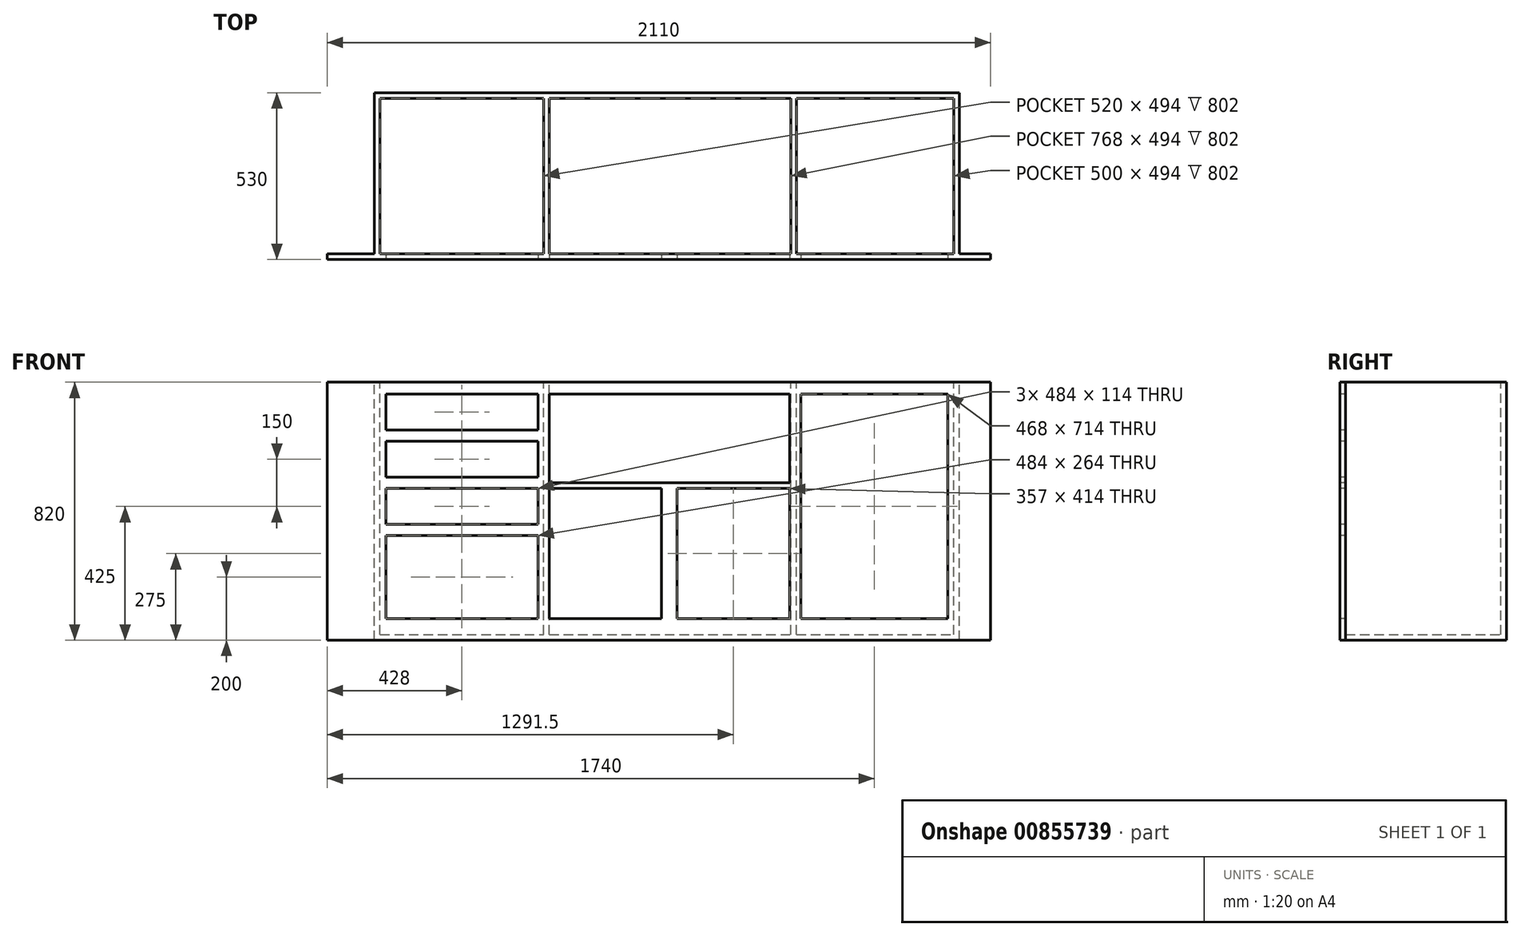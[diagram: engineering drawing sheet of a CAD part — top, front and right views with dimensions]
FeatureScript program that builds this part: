
annotation { "Feature Type Name" : "Feature", "Feature Type Description" : "" }
export const myFeature = defineFeature(function(context is Context, id is Id, definition is map)
    precondition{}
    {
        {
            var Q0;
            Q0=qCreatedBy(makeId("Top.planeOp"),FACE);
            var sketch = newSketch(context, id + "F0", { "sketchPlane" : qUnion([Q0])});
            skLineSegment(sketch, "E0.bottom", {"start": v(0, 0) * mm, "end": v(1860, 0) * mm});
            skLineSegment(sketch, "E0.top", {"start": v(0, 530) * mm, "end": v(1860, 530) * mm});
            skLineSegment(sketch, "E0.left", {"start": v(0, 18) * mm, "end": v(0, 530) * mm});
            skLineSegment(sketch, "E0.right", {"start": v(1860, 18) * mm, "end": v(1860, 530) * mm});
            skLineSegment(sketch, "E1.0", {"start": v(1842, 18) * mm, "end": v(1842, 512) * mm});
            skLineSegment(sketch, "E1.1", {"start": v(18, 18) * mm, "end": v(538, 18) * mm});
            skLineSegment(sketch, "E1.2", {"start": v(18, 18) * mm, "end": v(18, 512) * mm});
            skLineSegment(sketch, "E1.3", {"start": v(18, 512) * mm, "end": v(538, 512) * mm});
            skLineSegment(sketch, "E2.left", {"start": v(538, 512) * mm, "end": v(538, 18) * mm});
            skLineSegment(sketch, "E2.right", {"start": v(556, 512) * mm, "end": v(556, 18) * mm});
            skLineSegment(sketch, "E3.trimOffspring", {"start": v(556, 18) * mm, "end": v(1324, 18) * mm});
            skLineSegment(sketch, "E4.left", {"start": v(1342, 512) * mm, "end": v(1342, 18) * mm});
            skLineSegment(sketch, "E4.right", {"start": v(1324, 512) * mm, "end": v(1324, 18) * mm});
            skLineSegment(sketch, "E5.trimOffspring", {"start": v(1342, 18) * mm, "end": v(1842, 18) * mm});
            skLineSegment(sketch, "E6", {"start": v(0, 18) * mm, "end": v(-150, 18) * mm});
            skLineSegment(sketch, "E7", {"start": v(-150, 18) * mm, "end": v(-150, 0) * mm});
            skLineSegment(sketch, "E8", {"start": v(-150, 0) * mm, "end": v(0, 0) * mm});
            skLineSegment(sketch, "E9", {"start": v(1860, 0) * mm, "end": v(1960, 0) * mm});
            skLineSegment(sketch, "E10", {"start": v(1960, 0) * mm, "end": v(1960, 18) * mm});
            skLineSegment(sketch, "E11", {"start": v(1960, 18) * mm, "end": v(1860, 18) * mm});
            skLineSegment(sketch, "E12.trimOffspring", {"start": v(556, 512) * mm, "end": v(1324, 512) * mm});
            skLineSegment(sketch, "E13.trimOffspring", {"start": v(1342, 512) * mm, "end": v(1842, 512) * mm});
            skSolve(sketch);
        }
        {
            var Q0;
            Q0=makeQuery(id+"F0.imprint","IMPRINT",FACE,{"disambiguationData":[TD([[makeQuery(id+"F0.imprint","IMPRINT",EDGE,{"derivedFrom":sQuery(id+"F0.wireOp",EDGE,"E0.bottom")}),1.0]])]});
            var Q1;
            Q1=makeQuery(id+"F0.imprint","IMPRINT",FACE,{"disambiguationData":[TD([[makeQuery(id+"F0.imprint","IMPRINT",EDGE,{"derivedFrom":sQuery(id+"F0.wireOp",EDGE,"E2.top")}),1.0]])]});
            var Q2;
            Q2=makeQuery(id+"F0.imprint","IMPRINT",FACE,{"disambiguationData":[TD([[makeQuery(id+"F0.imprint","IMPRINT",EDGE,{"derivedFrom":sQuery(id+"F0.wireOp",EDGE,"E4.top")}),-1.0]])]});
            extrude(context, id + "F1", {"entities" : qUnion([Q0, Q1, Q2]), "oppositeDirection" : true, "depth" : (870 - 50) * mm, "offsetDistance" : 25 * mm});
        }
        {
            var Q0;
            Q0=makeQuery(id+"F1.opExtrude","SWEPT_FACE",FACE,{"disambiguationData":[OSD([sQuery(id+"F0.wireOp",EDGE,"E0.bottom"),sQuery(id+"F0.wireOp",EDGE,"E8"),sQuery(id+"F0.wireOp",EDGE,"E9")])]});
            var sketch = newSketch(context, id + "F2", { "sketchPlane" : qUnion([Q0])});
            skLineSegment(sketch, "E14", {"start": v(18, -20) * mm, "end": v(538, -20) * mm});
            skLineSegment(sketch, "E15", {"start": v(1842, -20) * mm, "end": v(1842, -770) * mm});
            skLineSegment(sketch, "E16", {"start": v(1842, -770) * mm, "end": v(1590, -770) * mm});
            skLineSegment(sketch, "E17", {"start": v(18, -20) * mm, "end": v(18, -170) * mm});
            skLineSegment(sketch, "E18", {"start": v(538, -20) * mm, "end": v(538, -170) * mm});
            skLineSegment(sketch, "E19", {"start": v(18, -170) * mm, "end": v(538, -170) * mm});
            skLineSegment(sketch, "E20", {"start": v(18, -320) * mm, "end": v(538, -320) * mm});
            skLineSegment(sketch, "E21", {"start": v(18, -470) * mm, "end": v(538, -470) * mm});
            skLineSegment(sketch, "E22", {"start": v(1338, -20) * mm, "end": v(1338, -770) * mm});
            skLineSegment(sketch, "E23.trimOffspring", {"start": v(1338, -20) * mm, "end": v(1590, -20) * mm});
            skLineSegment(sketch, "E24", {"start": v(538, -20) * mm, "end": v(938, -20) * mm});
            skLineSegment(sketch, "E25", {"start": v(538, -770) * mm, "end": v(18, -770) * mm});
            skLineSegment(sketch, "E26", {"start": v(913, -770) * mm, "end": v(538, -770) * mm});
            skLineSegment(sketch, "E27", {"start": v(1590, -770) * mm, "end": v(1338, -770) * mm});
            skLineSegment(sketch, "E28", {"start": v(1338, -770) * mm, "end": v(1338, -770) * mm});
            skLineSegment(sketch, "E29", {"start": v(538, -170) * mm, "end": v(538, -320) * mm});
            skLineSegment(sketch, "E30", {"start": v(538, -320) * mm, "end": v(538, -470) * mm});
            skLineSegment(sketch, "E31", {"start": v(538, -470) * mm, "end": v(538, -770) * mm});
            skLineSegment(sketch, "E32", {"start": v(18, -470) * mm, "end": v(18, -770) * mm});
            skLineSegment(sketch, "E33", {"start": v(18, -320) * mm, "end": v(18, -470) * mm});
            skLineSegment(sketch, "E34", {"start": v(18, -170) * mm, "end": v(18, -320) * mm});
            skLineSegment(sketch, "E35.0", {"start": v(36, -152) * mm, "end": v(520, -152) * mm});
            skLineSegment(sketch, "E35.1", {"start": v(36, -38) * mm, "end": v(36, -152) * mm});
            skLineSegment(sketch, "E35.2", {"start": v(36, -38) * mm, "end": v(520, -38) * mm});
            skLineSegment(sketch, "E35.3", {"start": v(520, -38) * mm, "end": v(520, -152) * mm});
            skLineSegment(sketch, "E36.0", {"start": v(36, -188) * mm, "end": v(520, -188) * mm});
            skLineSegment(sketch, "E36.1", {"start": v(36, -188) * mm, "end": v(36, -302) * mm});
            skLineSegment(sketch, "E36.2", {"start": v(36, -302) * mm, "end": v(520, -302) * mm});
            skLineSegment(sketch, "E36.3", {"start": v(520, -188) * mm, "end": v(520, -302) * mm});
            skLineSegment(sketch, "E37.0", {"start": v(36, -338) * mm, "end": v(36, -452) * mm});
            skLineSegment(sketch, "E37.1", {"start": v(36, -338) * mm, "end": v(520, -338) * mm});
            skLineSegment(sketch, "E37.2", {"start": v(520, -338) * mm, "end": v(520, -452) * mm});
            skLineSegment(sketch, "E37.3", {"start": v(36, -452) * mm, "end": v(520, -452) * mm});
            skLineSegment(sketch, "E38.0", {"start": v(36, -488) * mm, "end": v(36, -752) * mm});
            skLineSegment(sketch, "E38.1", {"start": v(36, -488) * mm, "end": v(520, -488) * mm});
            skLineSegment(sketch, "E38.2", {"start": v(520, -488) * mm, "end": v(520, -752) * mm});
            skLineSegment(sketch, "E38.3", {"start": v(520, -752) * mm, "end": v(36, -752) * mm});
            skLineSegment(sketch, "E39", {"start": v(938, -20) * mm, "end": v(1338, -20) * mm});
            skLineSegment(sketch, "E40", {"start": v(1338, -770) * mm, "end": v(913, -770) * mm});
            skLineSegment(sketch, "E41", {"start": v(1590, -20) * mm, "end": v(1842, -20) * mm});
            skLineSegment(sketch, "E42.0", {"start": v(556, -38) * mm, "end": v(556, -257.29) * mm});
            skLineSegment(sketch, "E42.1", {"start": v(556, -257.29) * mm, "end": v(556, -320) * mm});
            skLineSegment(sketch, "E42.2", {"start": v(913, -338) * mm, "end": v(913, -752) * mm});
            skLineSegment(sketch, "E42.4", {"start": v(556, -557.29) * mm, "end": v(556, -752) * mm});
            skLineSegment(sketch, "E42.5", {"start": v(556, -38) * mm, "end": v(913, -38) * mm});
            skLineSegment(sketch, "E42.6", {"start": v(556, -320) * mm, "end": v(556, -407.29) * mm});
            skLineSegment(sketch, "E43.0", {"start": v(1320, -752) * mm, "end": v(963, -752) * mm});
            skLineSegment(sketch, "E43.1", {"start": v(1320, -38) * mm, "end": v(1320, -320) * mm});
            skLineSegment(sketch, "E43.2", {"start": v(913, -38) * mm, "end": v(1320, -38) * mm});
            skLineSegment(sketch, "E43.3", {"start": v(963, -338) * mm, "end": v(963, -752) * mm});
            skLineSegment(sketch, "E44.0", {"start": v(1356, -38) * mm, "end": v(1356, -752) * mm});
            skLineSegment(sketch, "E44.1", {"start": v(1356, -38) * mm, "end": v(1572, -38) * mm});
            skLineSegment(sketch, "E44.3", {"start": v(1572, -752) * mm, "end": v(1356, -752) * mm});
            skLineSegment(sketch, "E45.0", {"start": v(1608, -38) * mm, "end": v(1824, -38) * mm});
            skLineSegment(sketch, "E45.2", {"start": v(1824, -752) * mm, "end": v(1608, -752) * mm});
            skLineSegment(sketch, "E45.3", {"start": v(1824, -38) * mm, "end": v(1824, -752) * mm});
            skLineSegment(sketch, "E46", {"start": v(556, -320) * mm, "end": v(1320, -320) * mm});
            skLineSegment(sketch, "E47", {"start": v(913, -338) * mm, "end": v(556, -338) * mm});
            skLineSegment(sketch, "E48", {"start": v(963, -338) * mm, "end": v(1320, -338) * mm});
            skLineSegment(sketch, "E49", {"start": v(556, -752) * mm, "end": v(913, -752) * mm});
            skLineSegment(sketch, "E50.trimOffspring", {"start": v(556, -338) * mm, "end": v(556, -557.29) * mm});
            skLineSegment(sketch, "E51.trimOffspring", {"start": v(1320, -338) * mm, "end": v(1320, -752) * mm});
            skLineSegment(sketch, "E52", {"start": v(1572, -38) * mm, "end": v(1608, -38) * mm});
            skLineSegment(sketch, "E53", {"start": v(1572, -752) * mm, "end": v(1608, -752) * mm});
            skLineSegment(sketch, "E54.bottom", {"start": v(538, -20) * mm, "end": v(1338, -20) * mm});
            skLineSegment(sketch, "E54.top", {"start": v(538, -320) * mm, "end": v(556, -320) * mm});
            skLineSegment(sketch, "E54.left", {"start": v(538, -20) * mm, "end": v(538, -320) * mm});
            skLineSegment(sketch, "E54.right", {"start": v(1338, -20) * mm, "end": v(1338, -320) * mm});
            skLineSegment(sketch, "E55", {"start": v(556, -320) * mm, "end": v(1338, -320) * mm});
            skLineSegment(sketch, "E56", {"start": v(556, -320) * mm, "end": v(556, -320) * mm});
            skSolve(sketch);
        }
        {
            var Q0;
            Q0=makeQuery(id+"F2.imprint","IMPRINT",FACE,{"disambiguationData":[TD([[makeQuery(id+"F2.imprint","IMPRINT",EDGE,{"derivedFrom":sQuery(id+"F2.wireOp",EDGE,"E35.0")}),1.0]])]});
            var Q1;
            Q1=makeQuery(id+"F2.imprint","IMPRINT",FACE,{"disambiguationData":[TD([[makeQuery(id+"F2.imprint","IMPRINT",EDGE,{"derivedFrom":sQuery(id+"F2.wireOp",EDGE,"E36.0")}),-1.0]])]});
            var Q2;
            Q2=makeQuery(id+"F2.imprint","IMPRINT",FACE,{"disambiguationData":[TD([[makeQuery(id+"F2.imprint","IMPRINT",EDGE,{"derivedFrom":sQuery(id+"F2.wireOp",EDGE,"E37.0")}),1.0]])]});
            var Q3;
            Q3=makeQuery(id+"F2.imprint","IMPRINT",FACE,{"disambiguationData":[TD([[makeQuery(id+"F2.imprint","IMPRINT",EDGE,{"derivedFrom":sQuery(id+"F2.wireOp",EDGE,"E38.0")}),1.0]])]});
            var Q4;
            Q4=makeQuery(id+"F2.imprint","IMPRINT",FACE,{"disambiguationData":[TD([[makeQuery(id+"F2.imprint","IMPRINT",EDGE,{"derivedFrom":sQuery(id+"F2.wireOp",EDGE,"E42.0")}),1.0]])]});
            var Q5;
            Q5=makeQuery(id+"F2.imprint","IMPRINT",FACE,{"disambiguationData":[TD([[makeQuery(id+"F2.imprint","IMPRINT",EDGE,{"derivedFrom":sQuery(id+"F2.wireOp",EDGE,"E43.0")}),-1.0]])]});
            var Q6;
            Q6=makeQuery(id+"F2.imprint","IMPRINT",FACE,{"disambiguationData":[TD([[makeQuery(id+"F2.imprint","IMPRINT",EDGE,{"derivedFrom":sQuery(id+"F2.wireOp",EDGE,"E44.0")}),1.0]])]});
            var Q7;
            Q7=makeQuery(id+"F2.imprint","IMPRINT",FACE,{"disambiguationData":[TD([[makeQuery(id+"F2.imprint","IMPRINT",EDGE,{"derivedFrom":sQuery(id+"F2.wireOp",EDGE,"E45.0")}),-1.0]])]});
            var Q8;
            Q8=makeQuery(id+"F2.imprint","IMPRINT",FACE,{"disambiguationData":[TD([[makeQuery(id+"F2.imprint","IMPRINT",EDGE,{"derivedFrom":sQuery(id+"F2.wireOp",EDGE,"E42.2")}),-1.0]])]});
            extrude(context, id + "F3", {"entities" : qUnion([Q0, Q1, Q2, Q3, Q4, Q5, Q6, Q7, Q8]), "operationType" : NewBodyOperationType.REMOVE, "oppositeDirection" : true, "depth" : 50 * mm, "offsetDistance" : 25 * mm});
        }
        {
            var Q0;
            Q0=makeQuery(id+"F1.opExtrude","CAP_FACE",FACE,{"disambiguationData":[OSD([sQuery(id+"F0.wireOp",EDGE,"E0.bottom"),sQuery(id+"F0.wireOp",EDGE,"E0.top"),sQuery(id+"F0.wireOp",EDGE,"E0.left"),sQuery(id+"F0.wireOp",EDGE,"E0.right"),sQuery(id+"F0.wireOp",EDGE,"E1.0"),sQuery(id+"F0.wireOp",EDGE,"E1.1"),sQuery(id+"F0.wireOp",EDGE,"E1.2"),sQuery(id+"F0.wireOp",EDGE,"E1.3"),sQuery(id+"F0.wireOp",EDGE,"E2.left"),sQuery(id+"F0.wireOp",EDGE,"E2.right"),sQuery(id+"F0.wireOp",EDGE,"E3.trimOffspring"),sQuery(id+"F0.wireOp",EDGE,"E4.left"),sQuery(id+"F0.wireOp",EDGE,"E4.right"),sQuery(id+"F0.wireOp",EDGE,"E5.trimOffspring"),sQuery(id+"F0.wireOp",EDGE,"E6"),sQuery(id+"F0.wireOp",EDGE,"E7"),sQuery(id+"F0.wireOp",EDGE,"E8"),sQuery(id+"F0.wireOp",EDGE,"E9"),sQuery(id+"F0.wireOp",EDGE,"E10"),sQuery(id+"F0.wireOp",EDGE,"E11"),sQuery(id+"F0.wireOp",EDGE,"E12.trimOffspring"),sQuery(id+"F0.wireOp",EDGE,"E13.trimOffspring")])],"isStart":false});
            var sketch = newSketch(context, id + "F4", { "sketchPlane" : qUnion([Q0])});
            skLineSegment(sketch, "E57.bottom", {"start": v(6.87, -7.8) * mm, "end": v(1842, -7.8) * mm});
            skLineSegment(sketch, "E57.top", {"start": v(6.87, -512) * mm, "end": v(1842, -512) * mm});
            skLineSegment(sketch, "E57.left", {"start": v(6.87, -7.8) * mm, "end": v(6.87, -512) * mm});
            skLineSegment(sketch, "E57.right", {"start": v(1842, -7.8) * mm, "end": v(1842, -512) * mm});
            skSolve(sketch);
        }
        {
            var Q0;
            Q0 = qSketchRegion(id + "F4", true);
            extrude(context, id + "F5", {"entities" : qUnion([Q0]), "operationType" : NewBodyOperationType.ADD, "oppositeDirection" : true, "depth" : 18 * mm, "offsetDistance" : 25 * mm});
        }
    });
